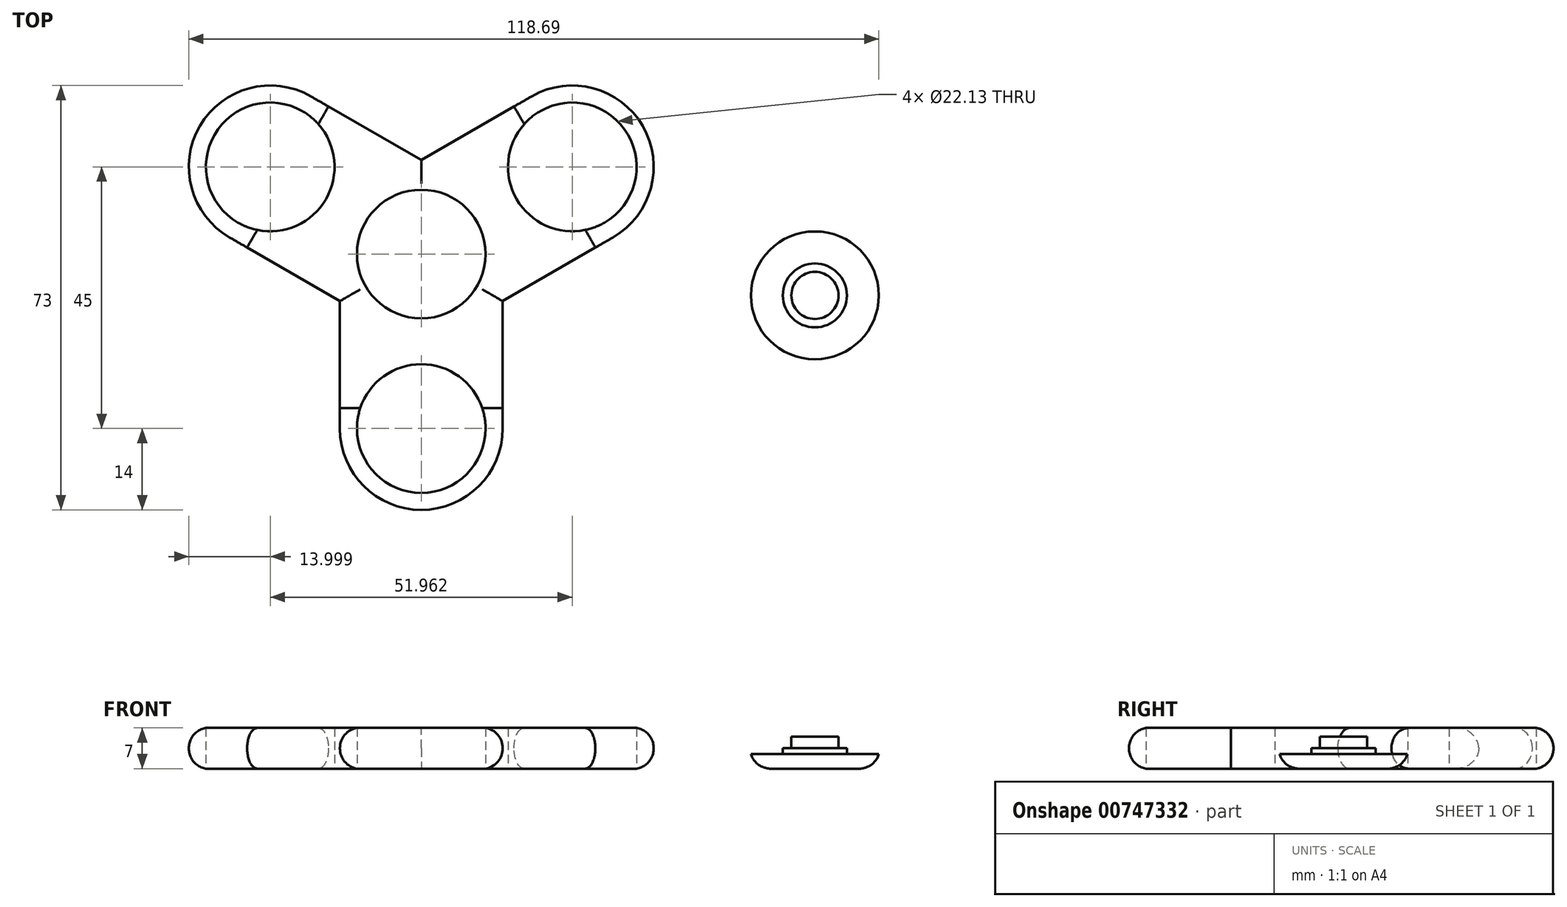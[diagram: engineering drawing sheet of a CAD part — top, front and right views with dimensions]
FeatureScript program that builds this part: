
annotation { "Feature Type Name" : "Feature", "Feature Type Description" : "" }
export const myFeature = defineFeature(function(context is Context, id is Id, definition is map)
    precondition{}
    {
        {
            var Q0;
            Q0=qCreatedBy(makeId("Top.planeOp"),FACE);
            var sketch = newSketch(context, id + "F0", { "sketchPlane" : qUnion([Q0])});
            skLineSegment(sketch, "E0.bottom", {"start": v(14, -15) * mm, "end": v(-14, -15) * mm});
            skLineSegment(sketch, "E0.top", {"start": v(14, 15) * mm, "end": v(-14, 15) * mm});
            skLineSegment(sketch, "E0.left", {"start": v(14, -15) * mm, "end": v(14, 15) * mm});
            skLineSegment(sketch, "E0.right", {"start": v(-14, -15) * mm, "end": v(-14, 15) * mm});
            skPoint(sketch, "E0.middle", {"position": v(0, 0) * mm});
            skCircle(sketch, "E1", {"center": v(0, 15) * mm, "radius": 14 * mm});
            skCircle(sketch, "E2", {"center": v(0, 15) * mm, "radius": 11.06 * mm});
            skCircle(sketch, "E3", {"center": v(0, -15) * mm, "radius": 14 * mm});
            skCircle(sketch, "E4", {"center": v(0, -15) * mm, "radius": 11.06 * mm});
            skSolve(sketch);
        }
        {
            var Q0;
            {var subQ0=sQuery(id+"F0.wireOp",EDGE,"E0.left");Q0=makeQuery(id+"F0.imprint","IMPRINT",FACE,{"disambiguationData":[TD([[makeQuery(id+"F0.imprint","IMPRINT",EDGE,{"derivedFrom":subQ0}),1.0]])]});}
            var Q1;
            {var subQ1=sQuery(id+"F0.wireOp",EDGE,"E0.bottom");var subQ3=sQuery(id+"F0.wireOp",EDGE,"E4");var subQ4=makeQuery(id+"F0.imprint","INTERSECT",VERTEX,{"disambiguationData":[OD(0.0)],"derivedFrom":[subQ1,subQ3]});Q1=makeQuery(id+"F0.imprint","IMPRINT",FACE,{"disambiguationData":[TD([[makeQuery(id+"F0.imprint","IMPRINT",EDGE,{"disambiguationData":[TD([[subQ4,1.0]])],"derivedFrom":subQ3}),-1.0]])]});}
            var Q2;
            {var subQ1=sQuery(id+"F0.wireOp",EDGE,"E0.top");var subQ3=sQuery(id+"F0.wireOp",EDGE,"E2");var subQ4=makeQuery(id+"F0.imprint","INTERSECT",VERTEX,{"disambiguationData":[OD(0.0)],"derivedFrom":[subQ1,subQ3]});Q2=makeQuery(id+"F0.imprint","IMPRINT",FACE,{"disambiguationData":[TD([[makeQuery(id+"F0.imprint","IMPRINT",EDGE,{"disambiguationData":[TD([[subQ4,-1.0]])],"derivedFrom":subQ3}),-1.0]])]});}
            var Q3;
            {var subQ1=sQuery(id+"F0.wireOp",EDGE,"E0.top");var subQ3=sQuery(id+"F0.wireOp",EDGE,"E2");var subQ4=makeQuery(id+"F0.imprint","INTERSECT",VERTEX,{"disambiguationData":[OD(0.0)],"derivedFrom":[subQ1,subQ3]});Q3=makeQuery(id+"F0.imprint","IMPRINT",FACE,{"disambiguationData":[TD([[makeQuery(id+"F0.imprint","IMPRINT",EDGE,{"disambiguationData":[TD([[subQ4,1.0]])],"derivedFrom":subQ3}),-1.0]])]});}
            var Q4;
            {var subQ1=sQuery(id+"F0.wireOp",EDGE,"E0.bottom");var subQ3=sQuery(id+"F0.wireOp",EDGE,"E4");var subQ4=makeQuery(id+"F0.imprint","INTERSECT",VERTEX,{"disambiguationData":[OD(0.0)],"derivedFrom":[subQ1,subQ3]});Q4=makeQuery(id+"F0.imprint","IMPRINT",FACE,{"disambiguationData":[TD([[makeQuery(id+"F0.imprint","IMPRINT",EDGE,{"disambiguationData":[TD([[subQ4,-1.0]])],"derivedFrom":subQ3}),-1.0]])]});}
            extrude(context, id + "F1", {"entities" : qUnion([Q0, Q1, Q2, Q3, Q4]), "depth" : 7 * mm, "offsetDistance" : 25.4 * mm});
        }
        {
            var Q0;
            Q0=makeQuery(id+"F1.opExtrude","SWEPT_BODY",BODY,{"disambiguationData":[OSD([sQuery(id+"F0.wireOp",EDGE,"E0.left"),sQuery(id+"F0.wireOp",EDGE,"E0.right"),sQuery(id+"F0.wireOp",EDGE,"E1"),sQuery(id+"F0.wireOp",EDGE,"E2"),sQuery(id+"F0.wireOp",EDGE,"E3"),sQuery(id+"F0.wireOp",EDGE,"E4")])]});
            var Q1;
            Q1=makeQuery(id+"F1.opExtrude","CAP_EDGE",EDGE,{"disambiguationData":[OSD([sQuery(id+"F0.wireOp",EDGE,"E2")])],"isStart":false});
            circularPattern(context, id + "F2", {"operationType" : NewBodyOperationType.ADD, "entities" : qUnion([Q0]), "axis" : qUnion([Q1]), "angle" : 360 * degree, "instanceCount" : 3, "equalSpace" : true});
        }
        {
            var Q0;
            Q0=qCreatedBy(makeId("Top.planeOp"),FACE);
            var sketch = newSketch(context, id + "F3", { "sketchPlane" : qUnion([Q0])});
            skCircle(sketch, "E5", {"center": v(67.71, 7.9) * mm, "radius": 11 * mm});
            skCircle(sketch, "E6", {"center": v(67.71, 7.9) * mm, "radius": 5.5 * mm});
            skCircle(sketch, "E7", {"center": v(67.71, 7.9) * mm, "radius": 4.05 * mm});
            skSolve(sketch);
        }
        {
            var Q0;
            Q0=makeQuery(id+"F3.imprint","IMPRINT",FACE,{"disambiguationData":[TD([[makeQuery(id+"F3.imprint","IMPRINT",EDGE,{"derivedFrom":sQuery(id+"F3.wireOp",EDGE,"E5")}),1.0]])]});
            extrude(context, id + "F4", {"entities" : qUnion([Q0]), "depth" : 2.5 * mm, "offsetDistance" : 25.4 * mm});
        }
        {
            var Q0;
            Q0=makeQuery(id+"F3.imprint","IMPRINT",FACE,{"disambiguationData":[TD([[makeQuery(id+"F3.imprint","IMPRINT",EDGE,{"derivedFrom":sQuery(id+"F3.wireOp",EDGE,"E6")}),1.0]])]});
            extrude(context, id + "F5", {"entities" : qUnion([Q0]), "operationType" : NewBodyOperationType.ADD, "depth" : 3.5 * mm, "offsetDistance" : 25.4 * mm});
        }
        {
            var Q0;
            Q0=makeQuery(id+"F3.imprint","IMPRINT",FACE,{"disambiguationData":[TD([[makeQuery(id+"F3.imprint","IMPRINT",EDGE,{"derivedFrom":sQuery(id+"F3.wireOp",EDGE,"E7")}),1.0]])]});
            extrude(context, id + "F6", {"entities" : qUnion([Q0]), "operationType" : NewBodyOperationType.ADD, "depth" : 5.5 * mm, "offsetDistance" : 25.4 * mm});
        }
        {
            var Q0;
            Q0=makeQuery(id+"F2.opPattern","COPY",EDGE,{"derivedFrom":makeQuery(id+"F1.opExtrude","CAP_EDGE",EDGE,{"disambiguationData":[OSD([sQuery(id+"F0.wireOp",EDGE,"E0.right")])],"isStart":false}),"instanceName":"1"});
            var Q1;
            Q1=makeQuery(id+"F2.opPattern","COPY",EDGE,{"derivedFrom":makeQuery(id+"F1.opExtrude","CAP_EDGE",EDGE,{"disambiguationData":[OSD([sQuery(id+"F0.wireOp",EDGE,"E3")])],"isStart":false}),"instanceName":"1"});
            var Q2;
            Q2=makeQuery(id+"F1.opExtrude","CAP_EDGE",EDGE,{"disambiguationData":[OSD([sQuery(id+"F0.wireOp",EDGE,"E3")])],"isStart":false});
            var Q3;
            Q3=makeQuery(id+"F1.opExtrude","CAP_EDGE",EDGE,{"disambiguationData":[OSD([sQuery(id+"F0.wireOp",EDGE,"E0.left")])],"isStart":false});
            var Q4;
            Q4=makeQuery(id+"F1.opExtrude","CAP_EDGE",EDGE,{"disambiguationData":[OSD([sQuery(id+"F0.wireOp",EDGE,"E0.right")])],"isStart":false});
            var Q5;
            Q5=makeQuery(id+"F2.opPattern","COPY",EDGE,{"derivedFrom":makeQuery(id+"F1.opExtrude","CAP_EDGE",EDGE,{"disambiguationData":[OSD([sQuery(id+"F0.wireOp",EDGE,"E0.left")])],"isStart":false}),"instanceName":"2"});
            var Q6;
            Q6=makeQuery(id+"F2.opPattern","COPY",EDGE,{"derivedFrom":makeQuery(id+"F1.opExtrude","CAP_EDGE",EDGE,{"disambiguationData":[OSD([sQuery(id+"F0.wireOp",EDGE,"E3")])],"isStart":false}),"instanceName":"2"});
            var Q7;
            Q7=makeQuery(id+"F2.opPattern","COPY",EDGE,{"derivedFrom":makeQuery(id+"F1.opExtrude","CAP_EDGE",EDGE,{"disambiguationData":[OSD([sQuery(id+"F0.wireOp",EDGE,"E0.left")])],"isStart":false}),"instanceName":"1"});
            var Q8;
            Q8=makeQuery(id+"F2.opPattern","COPY",EDGE,{"derivedFrom":makeQuery(id+"F1.opExtrude","CAP_EDGE",EDGE,{"disambiguationData":[OSD([sQuery(id+"F0.wireOp",EDGE,"E0.right")])],"isStart":false}),"instanceName":"2"});
            fillet(context, id + "F7", {"entities" : qUnion([Q0, Q1, Q2, Q3, Q4, Q5, Q6, Q7, Q8]), "radius" : 3.5 * mm, "tangentPropagation" : true, "allowEdgeOverflow" : false});
        }
        {
            var Q0;
            Q0=makeQuery(id+"F2.opPattern","COPY",EDGE,{"derivedFrom":makeQuery(id+"F1.opExtrude","CAP_EDGE",EDGE,{"disambiguationData":[OSD([sQuery(id+"F0.wireOp",EDGE,"E0.right")])],"isStart":true}),"instanceName":"2"});
            var Q1;
            Q1=makeQuery(id+"F2.opPattern","COPY",EDGE,{"derivedFrom":makeQuery(id+"F1.opExtrude","CAP_EDGE",EDGE,{"disambiguationData":[OSD([sQuery(id+"F0.wireOp",EDGE,"E0.left")])],"isStart":true}),"instanceName":"1"});
            var Q2;
            Q2=makeQuery(id+"F2.opPattern","COPY",EDGE,{"derivedFrom":makeQuery(id+"F1.opExtrude","CAP_EDGE",EDGE,{"disambiguationData":[OSD([sQuery(id+"F0.wireOp",EDGE,"E0.left")])],"isStart":true}),"instanceName":"2"});
            var Q3;
            Q3=makeQuery(id+"F2.opPattern","COPY",EDGE,{"derivedFrom":makeQuery(id+"F1.opExtrude","CAP_EDGE",EDGE,{"disambiguationData":[OSD([sQuery(id+"F0.wireOp",EDGE,"E0.right")])],"isStart":true}),"instanceName":"1"});
            var Q4;
            Q4=makeQuery(id+"F1.opExtrude","CAP_EDGE",EDGE,{"disambiguationData":[OSD([sQuery(id+"F0.wireOp",EDGE,"E0.left")])],"isStart":true});
            var Q5;
            Q5=makeQuery(id+"F2.opPattern","COPY",EDGE,{"derivedFrom":makeQuery(id+"F1.opExtrude","CAP_EDGE",EDGE,{"disambiguationData":[OSD([sQuery(id+"F0.wireOp",EDGE,"E3")])],"isStart":true}),"instanceName":"2"});
            var Q6;
            Q6=makeQuery(id+"F1.opExtrude","CAP_EDGE",EDGE,{"disambiguationData":[OSD([sQuery(id+"F0.wireOp",EDGE,"E3")])],"isStart":true});
            var Q7;
            Q7=makeQuery(id+"F1.opExtrude","CAP_EDGE",EDGE,{"disambiguationData":[OSD([sQuery(id+"F0.wireOp",EDGE,"E0.right")])],"isStart":true});
            var Q8;
            Q8=makeQuery(id+"F2.opPattern","COPY",EDGE,{"derivedFrom":makeQuery(id+"F1.opExtrude","CAP_EDGE",EDGE,{"disambiguationData":[OSD([sQuery(id+"F0.wireOp",EDGE,"E3")])],"isStart":true}),"instanceName":"1"});
            fillet(context, id + "F8", {"entities" : qUnion([Q0, Q1, Q2, Q3, Q4, Q5, Q6, Q7, Q8]), "radius" : 3.5 * mm, "tangentPropagation" : true, "allowEdgeOverflow" : false});
        }
        {
            var Q0;
            Q0=makeQuery(id+"F4.opExtrude","CAP_EDGE",EDGE,{"disambiguationData":[OSD([sQuery(id+"F3.wireOp",EDGE,"E5")])],"isStart":true});
            fillet(context, id + "F9", {"entities" : qUnion([Q0]), "radius" : 3.5 * mm, "tangentPropagation" : true, "allowEdgeOverflow" : false});
        }
    });
